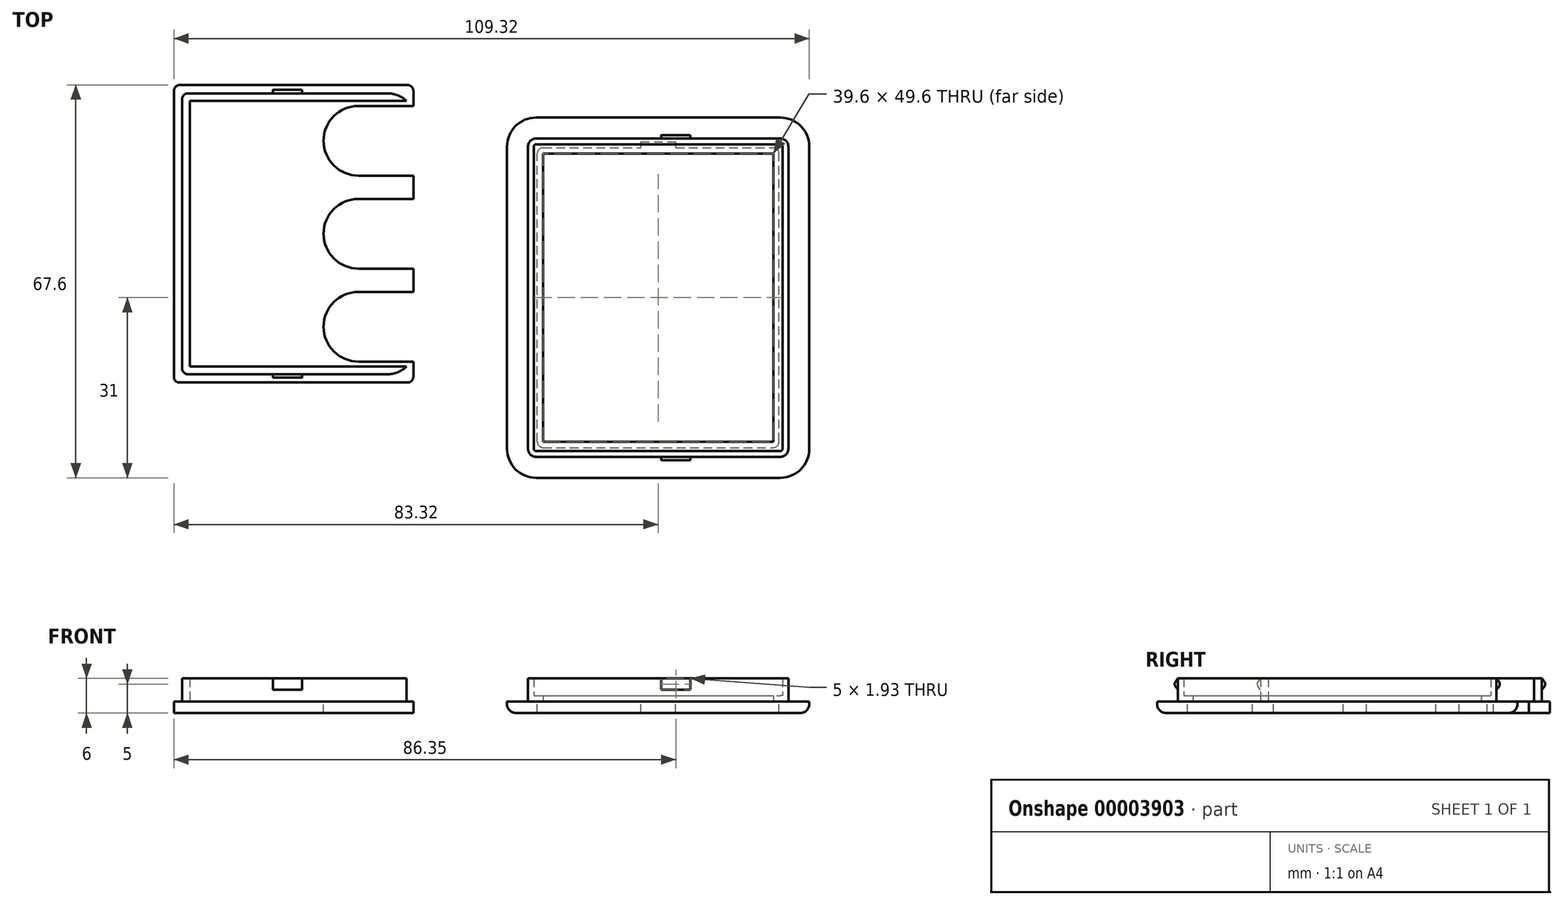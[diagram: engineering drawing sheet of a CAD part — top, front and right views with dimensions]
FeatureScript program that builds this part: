
annotation { "Feature Type Name" : "Feature", "Feature Type Description" : "" }
export const myFeature = defineFeature(function(context is Context, id is Id, definition is map)
    precondition{}
    {
        {
            var Q0;
            Q0=qCreatedBy(makeId("Top.planeOp"),FACE);
            var sketch = newSketch(context, id + "F0", { "sketchPlane" : qUnion([Q0])});
            skLineSegment(sketch, "E0.bottom", {"start": v(5, 0) * mm, "end": v(47, 0) * mm});
            skLineSegment(sketch, "E0.top", {"start": v(5, 62) * mm, "end": v(47, 62) * mm});
            skLineSegment(sketch, "E0.left", {"start": v(0, 5) * mm, "end": v(0, 57) * mm});
            skLineSegment(sketch, "E0.right", {"start": v(52, 5) * mm, "end": v(52, 57) * mm});
            skLineSegment(sketch, "E1.0", {"start": v(6.2, 56.8) * mm, "end": v(45.8, 56.8) * mm});
            skLineSegment(sketch, "E1.1", {"start": v(5.2, 6.2) * mm, "end": v(5.2, 55.8) * mm});
            skLineSegment(sketch, "E1.2", {"start": v(6.2, 5.2) * mm, "end": v(45.8, 5.2) * mm});
            skLineSegment(sketch, "E1.3", {"start": v(46.8, 6.2) * mm, "end": v(46.8, 55.8) * mm});
            skLineSegment(sketch, "E2.0", {"start": v(6.2, 55.8) * mm, "end": v(45.8, 55.8) * mm});
            skLineSegment(sketch, "E2.1", {"start": v(6.2, 6.2) * mm, "end": v(6.2, 55.8) * mm});
            skLineSegment(sketch, "E2.2", {"start": v(6.2, 6.2) * mm, "end": v(45.8, 6.2) * mm});
            skLineSegment(sketch, "E2.3", {"start": v(45.8, 6.2) * mm, "end": v(45.8, 55.8) * mm});
            skPoint(sketch, "E3.visualSharp", {"position": v(0, 62) * mm});
            skArc(sketch, "E3.filletArc", {"start": v(5, 62) * mm, "mid": v(1.46, 60.54) * mm, "end": v(0, 57) * mm});
            skPoint(sketch, "E4.visualSharp", {"position": v(52, 62) * mm});
            skArc(sketch, "E4.filletArc", {"start": v(52, 57) * mm, "mid": v(50.54, 60.54) * mm, "end": v(47, 62) * mm});
            skPoint(sketch, "E5.visualSharp", {"position": v(52, 0) * mm});
            skArc(sketch, "E5.filletArc", {"start": v(47, 0) * mm, "mid": v(50.54, 1.46) * mm, "end": v(52, 5) * mm});
            skPoint(sketch, "E6.visualSharp", {"position": v(0, 0) * mm});
            skArc(sketch, "E6.filletArc", {"start": v(0, 5) * mm, "mid": v(1.46, 1.46) * mm, "end": v(5, 0) * mm});
            skPoint(sketch, "E7.visualSharp", {"position": v(5.2, 56.8) * mm});
            skArc(sketch, "E7.filletArc", {"start": v(6.2, 56.8) * mm, "mid": v(5.5, 56.5) * mm, "end": v(5.2, 55.8) * mm});
            skPoint(sketch, "E8.visualSharp", {"position": v(46.8, 56.8) * mm});
            skArc(sketch, "E8.filletArc", {"start": v(46.8, 55.8) * mm, "mid": v(46.5, 56.5) * mm, "end": v(45.8, 56.8) * mm});
            skPoint(sketch, "E9.visualSharp", {"position": v(5.2, 5.2) * mm});
            skArc(sketch, "E9.filletArc", {"start": v(5.2, 6.2) * mm, "mid": v(5.5, 5.5) * mm, "end": v(6.2, 5.2) * mm});
            skPoint(sketch, "E10.visualSharp", {"position": v(46.8, 5.2) * mm});
            skArc(sketch, "E10.filletArc", {"start": v(45.8, 5.2) * mm, "mid": v(46.5, 5.5) * mm, "end": v(46.8, 6.2) * mm});
            skLineSegment(sketch, "E11", {"start": v(23, 56.8) * mm, "end": v(23, 57.85) * mm});
            skLineSegment(sketch, "E12", {"start": v(23, 57.85) * mm, "end": v(29, 57.85) * mm});
            skLineSegment(sketch, "E13", {"start": v(29, 57.85) * mm, "end": v(29, 56.8) * mm});
            skLineSegment(sketch, "E14", {"start": v(23, 57.85) * mm, "end": v(5.2, 57.85) * mm, "construction": true});
            skLineSegment(sketch, "E15", {"start": v(29, 57.85) * mm, "end": v(46.8, 57.85) * mm, "construction": true});
            skArc(sketch, "E16.0", {"start": v(5, 58.4) * mm, "mid": v(4.01, 57.99) * mm, "end": v(3.6, 57) * mm});
            skLineSegment(sketch, "E16.1", {"start": v(3.6, 5) * mm, "end": v(3.6, 57) * mm});
            skArc(sketch, "E16.2", {"start": v(3.6, 5) * mm, "mid": v(4.01, 4.01) * mm, "end": v(5, 3.6) * mm});
            skLineSegment(sketch, "E16.3", {"start": v(5, 3.6) * mm, "end": v(47, 3.6) * mm});
            skArc(sketch, "E16.4", {"start": v(47, 3.6) * mm, "mid": v(47.99, 4.01) * mm, "end": v(48.4, 5) * mm});
            skLineSegment(sketch, "E16.5", {"start": v(5, 58.4) * mm, "end": v(47, 58.4) * mm});
            skLineSegment(sketch, "E16.6", {"start": v(48.4, 5) * mm, "end": v(48.4, 57) * mm});
            skArc(sketch, "E16.7", {"start": v(48.4, 57) * mm, "mid": v(47.99, 57.99) * mm, "end": v(47, 58.4) * mm});
            skLineSegment(sketch, "E17.0", {"start": v(5, 57.4) * mm, "end": v(47, 57.4) * mm});
            skArc(sketch, "E17.1", {"start": v(47.4, 57) * mm, "mid": v(47.28, 57.28) * mm, "end": v(47, 57.4) * mm});
            skLineSegment(sketch, "E17.2", {"start": v(47.4, 5) * mm, "end": v(47.4, 57) * mm});
            skArc(sketch, "E17.3", {"start": v(47, 4.6) * mm, "mid": v(47.28, 4.72) * mm, "end": v(47.4, 5) * mm});
            skLineSegment(sketch, "E17.4", {"start": v(5, 4.6) * mm, "end": v(47, 4.6) * mm});
            skArc(sketch, "E17.5", {"start": v(5, 57.4) * mm, "mid": v(4.72, 57.28) * mm, "end": v(4.6, 57) * mm});
            skArc(sketch, "E17.6", {"start": v(4.6, 5) * mm, "mid": v(4.72, 4.72) * mm, "end": v(5, 4.6) * mm});
            skLineSegment(sketch, "E17.7", {"start": v(4.6, 5) * mm, "end": v(4.6, 57) * mm});
            skSolve(sketch);
        }
        {
            var Q0;
            {var subQ7=sQuery(id+"F0.wireOp",EDGE,"E12");Q0=makeQuery(id+"F0.imprint","IMPRINT",FACE,{"disambiguationData":[TD([[makeQuery(id+"F0.imprint","IMPRINT",EDGE,{"derivedFrom":subQ7}),1.0]])]});}
            var Q1;
            {var subQ5=sQuery(id+"F0.wireOp",EDGE,"E12");Q1=makeQuery(id+"F0.imprint","IMPRINT",FACE,{"disambiguationData":[TD([[makeQuery(id+"F0.imprint","IMPRINT",EDGE,{"derivedFrom":subQ5}),-1.0]])]});}
            extrude(context, id + "F1", {"entities" : qUnion([Q0, Q1]), "depth" : 4 * mm});
        }
        {
            var Q0;
            Q0=makeQuery(id+"F0.imprint","IMPRINT",FACE,{"disambiguationData":[TD([[makeQuery(id+"F0.imprint","IMPRINT",EDGE,{"derivedFrom":sQuery(id+"F0.wireOp",EDGE,"E0.bottom")}),1.0]])]});
            var Q1;
            {var subQ7=sQuery(id+"F0.wireOp",EDGE,"E12");Q1=makeQuery(id+"F0.imprint","IMPRINT",FACE,{"disambiguationData":[TD([[makeQuery(id+"F0.imprint","IMPRINT",EDGE,{"derivedFrom":subQ7}),1.0]])]});}
            var Q2;
            Q2=makeQuery(id+"F0.imprint","IMPRINT",FACE,{"disambiguationData":[TD([[makeQuery(id+"F0.imprint","IMPRINT",EDGE,{"derivedFrom":sQuery(id+"F0.wireOp",EDGE,"E1.1")}),1.0]])]});
            extrude(context, id + "F2", {"entities" : qUnion([Q0, Q1, Q2]), "operationType" : NewBodyOperationType.ADD, "oppositeDirection" : true, "depth" : 1.96 * mm});
        }
        {
            var Q0;
            Q0=makeQuery(id+"F2.opExtrude","CAP_EDGE",EDGE,{"disambiguationData":[OSD([sQuery(id+"F0.wireOp",EDGE,"E0.top")])],"isStart":false});
            var Q1;
            Q1=makeQuery(id+"F2.opExtrude","CAP_EDGE",EDGE,{"disambiguationData":[OSD([sQuery(id+"F0.wireOp",EDGE,"E4.filletArc")])],"isStart":false});
            var Q2;
            Q2=makeQuery(id+"F2.opExtrude","CAP_EDGE",EDGE,{"disambiguationData":[OSD([sQuery(id+"F0.wireOp",EDGE,"E0.right")])],"isStart":false});
            var Q3;
            Q3=makeQuery(id+"F2.opExtrude","CAP_EDGE",EDGE,{"disambiguationData":[OSD([sQuery(id+"F0.wireOp",EDGE,"E5.filletArc")])],"isStart":false});
            var Q4;
            Q4=makeQuery(id+"F2.opExtrude","CAP_EDGE",EDGE,{"disambiguationData":[OSD([sQuery(id+"F0.wireOp",EDGE,"E0.bottom")])],"isStart":false});
            var Q5;
            Q5=makeQuery(id+"F2.opExtrude","CAP_EDGE",EDGE,{"disambiguationData":[OSD([sQuery(id+"F0.wireOp",EDGE,"E3.filletArc")])],"isStart":false});
            var Q6;
            Q6=makeQuery(id+"F2.opExtrude","CAP_EDGE",EDGE,{"disambiguationData":[OSD([sQuery(id+"F0.wireOp",EDGE,"E0.left")])],"isStart":false});
            var Q7;
            Q7=makeQuery(id+"F2.opExtrude","CAP_EDGE",EDGE,{"disambiguationData":[OSD([sQuery(id+"F0.wireOp",EDGE,"E6.filletArc")])],"isStart":false});
            fillet(context, id + "F3", {"entities" : qUnion([Q0, Q1, Q2, Q3, Q4, Q5, Q6, Q7]), "radius" : 1.5 * mm, "tangentPropagation" : true, "allowEdgeOverflow" : false});
        }
        {
            var Q0;
            Q0=makeQuery(id+"F0.imprint","IMPRINT",FACE,{"disambiguationData":[TD([[makeQuery(id+"F0.imprint","IMPRINT",EDGE,{"derivedFrom":sQuery(id+"F0.wireOp",EDGE,"E1.1")}),-1.0]])]});
            var Q1;
            Q1=makeQuery(id+"F0.imprint","IMPRINT",FACE,{"disambiguationData":[TD([[makeQuery(id+"F0.imprint","IMPRINT",EDGE,{"derivedFrom":sQuery(id+"F0.wireOp",EDGE,"E1.1")}),1.0]])]});
            var Q2;
            {var subQ3=sQuery(id+"F0.wireOp",EDGE,"E11");var subQ5=sQuery(id+"F0.wireOp",EDGE,"E1.0");var subQ7=makeQuery(id+"F0.imprint","INTERSECT",VERTEX,{"derivedFrom":[subQ5,subQ3]});Q2=makeQuery(id+"F0.imprint","IMPRINT",FACE,{"disambiguationData":[TD([[makeQuery(id+"F0.imprint","IMPRINT",EDGE,{"disambiguationData":[TD([[subQ7,-1.0]])],"derivedFrom":subQ5}),1.0]])]});}
            extrude(context, id + "F4", {"entities" : qUnion([Q0, Q1, Q2]), "operationType" : NewBodyOperationType.ADD, "depth" : 1 * mm});
        }
        {
            var Q0;
            Q0=qCreatedBy(makeId("Top.planeOp"),FACE);
            var sketch = newSketch(context, id + "F5", { "sketchPlane" : qUnion([Q0])});
            skLineSegment(sketch, "E18.bottom", {"start": v(-56.32, 16.4) * mm, "end": v(-17.12, 16.4) * mm});
            skLineSegment(sketch, "E18.top", {"start": v(-56.32, 67.6) * mm, "end": v(-17.12, 67.6) * mm});
            skLineSegment(sketch, "E18.left", {"start": v(-57.32, 17.4) * mm, "end": v(-57.32, 66.6) * mm});
            skLineSegment(sketch, "E18.right", {"start": v(-16.12, 17.4) * mm, "end": v(-16.12, 66.6) * mm});
            skLineSegment(sketch, "E19.0", {"start": v(-55.24, 18.47) * mm, "end": v(-55.24, 65.52) * mm, "construction": true});
            skLineSegment(sketch, "E19.1", {"start": v(-55.24, 18.47) * mm, "end": v(-17.29, 18.47) * mm, "construction": true});
            skLineSegment(sketch, "E19.3", {"start": v(-55.24, 65.52) * mm, "end": v(-17.29, 65.52) * mm, "construction": true});
            skLineSegment(sketch, "E20.0", {"start": v(-54.6, 64.87) * mm, "end": v(-17.29, 64.87) * mm});
            skLineSegment(sketch, "E20.1", {"start": v(-54.6, 19.12) * mm, "end": v(-54.6, 64.87) * mm});
            skLineSegment(sketch, "E20.2", {"start": v(-54.6, 19.12) * mm, "end": v(-17.29, 19.12) * mm});
            skLineSegment(sketch, "E21.0", {"start": v(-54.9, 66.17) * mm, "end": v(-17.29, 66.17) * mm});
            skLineSegment(sketch, "E21.1", {"start": v(-55.9, 18.82) * mm, "end": v(-55.9, 65.17) * mm});
            skLineSegment(sketch, "E21.2", {"start": v(-54.9, 17.82) * mm, "end": v(-17.29, 17.82) * mm});
            skLineSegment(sketch, "E22", {"start": v(-17.29, 17.82) * mm, "end": v(-17.29, 19.12) * mm});
            skLineSegment(sketch, "E23", {"start": v(-17.29, 64.87) * mm, "end": v(-17.29, 66.17) * mm});
            skLineSegment(sketch, "E24", {"start": v(-57.32, 42) * mm, "end": v(-31.57, 42) * mm, "construction": true});
            skLineSegment(sketch, "E25.bottom", {"start": v(-25.57, 36) * mm, "end": v(-16.12, 36) * mm});
            skLineSegment(sketch, "E25.top", {"start": v(-25.57, 48) * mm, "end": v(-16.12, 48) * mm});
            skLineSegment(sketch, "E25.left", {"start": v(-31.57, 42) * mm, "end": v(-31.57, 42) * mm});
            skLineSegment(sketch, "E25.right", {"start": v(-16.12, 36) * mm, "end": v(-16.12, 48) * mm});
            skLineSegment(sketch, "E26.1.0.0", {"start": v(-31.57, 26) * mm, "end": v(-31.57, 26) * mm});
            skLineSegment(sketch, "E26.1.0.1", {"start": v(-25.57, 20) * mm, "end": v(-16.12, 20) * mm});
            skLineSegment(sketch, "E26.1.0.2", {"start": v(-25.57, 32) * mm, "end": v(-16.12, 32) * mm});
            skLineSegment(sketch, "E26.direction1", {"start": v(-31.57, 36) * mm, "end": v(-31.57, 20) * mm, "construction": true});
            skLineSegment(sketch, "E27.1.0.0", {"start": v(-31.57, 58) * mm, "end": v(-31.57, 58) * mm});
            skLineSegment(sketch, "E27.1.0.1", {"start": v(-25.57, 52) * mm, "end": v(-16.12, 52) * mm});
            skLineSegment(sketch, "E27.1.0.2", {"start": v(-25.57, 64) * mm, "end": v(-16.12, 64) * mm});
            skLineSegment(sketch, "E27.direction1", {"start": v(-31.57, 36) * mm, "end": v(-31.57, 52) * mm, "construction": true});
            skPoint(sketch, "E28.visualSharp", {"position": v(-31.57, 20) * mm});
            skArc(sketch, "E28.filletArc", {"start": v(-31.57, 26) * mm, "mid": v(-29.8, 21.75) * mm, "end": v(-25.57, 20) * mm});
            skPoint(sketch, "E29.visualSharp", {"position": v(-31.57, 32) * mm});
            skArc(sketch, "E29.filletArc", {"start": v(-25.57, 32) * mm, "mid": v(-29.8, 30.24) * mm, "end": v(-31.57, 26) * mm});
            skPoint(sketch, "E30.visualSharp", {"position": v(-31.57, 36) * mm});
            skArc(sketch, "E30.filletArc", {"start": v(-31.57, 42) * mm, "mid": v(-29.8, 37.75) * mm, "end": v(-25.57, 36) * mm});
            skPoint(sketch, "E31.visualSharp", {"position": v(-31.57, 48) * mm});
            skArc(sketch, "E31.filletArc", {"start": v(-25.57, 48) * mm, "mid": v(-29.8, 46.24) * mm, "end": v(-31.57, 42) * mm});
            skPoint(sketch, "E32.visualSharp", {"position": v(-31.57, 52) * mm});
            skArc(sketch, "E32.filletArc", {"start": v(-31.57, 58) * mm, "mid": v(-29.8, 53.75) * mm, "end": v(-25.57, 52) * mm});
            skPoint(sketch, "E33.visualSharp", {"position": v(-31.57, 64) * mm});
            skArc(sketch, "E33.filletArc", {"start": v(-25.57, 64) * mm, "mid": v(-29.8, 62.24) * mm, "end": v(-31.57, 58) * mm});
            skPoint(sketch, "E34.visualSharp", {"position": v(-57.32, 16.4) * mm});
            skArc(sketch, "E34.filletArc", {"start": v(-57.32, 17.4) * mm, "mid": v(-57.02, 16.7) * mm, "end": v(-56.32, 16.4) * mm});
            skPoint(sketch, "E35.visualSharp", {"position": v(-16.12, 16.4) * mm});
            skArc(sketch, "E35.filletArc", {"start": v(-17.12, 16.4) * mm, "mid": v(-16.4, 16.7) * mm, "end": v(-16.12, 17.4) * mm});
            skPoint(sketch, "E36.visualSharp", {"position": v(-57.32, 67.6) * mm});
            skArc(sketch, "E36.filletArc", {"start": v(-56.32, 67.6) * mm, "mid": v(-57.02, 67.3) * mm, "end": v(-57.32, 66.6) * mm});
            skPoint(sketch, "E37.visualSharp", {"position": v(-16.12, 67.6) * mm});
            skArc(sketch, "E37.filletArc", {"start": v(-16.12, 66.6) * mm, "mid": v(-16.4, 67.3) * mm, "end": v(-17.12, 67.6) * mm});
            skPoint(sketch, "E38.visualSharp", {"position": v(-55.9, 66.17) * mm});
            skArc(sketch, "E38.filletArc", {"start": v(-54.9, 66.17) * mm, "mid": v(-55.6, 65.88) * mm, "end": v(-55.9, 65.17) * mm});
            skPoint(sketch, "E39.visualSharp", {"position": v(-55.9, 17.82) * mm});
            skArc(sketch, "E39.filletArc", {"start": v(-55.9, 18.82) * mm, "mid": v(-55.6, 18.12) * mm, "end": v(-54.9, 17.82) * mm});
            skSolve(sketch);
        }
        {
            var Q0;
            Q0=makeQuery(id+"F5.imprint","IMPRINT",FACE,{"disambiguationData":[TD([[makeQuery(id+"F5.imprint","IMPRINT",EDGE,{"derivedFrom":sQuery(id+"F5.wireOp",EDGE,"E20.0")}),1.0]])]});
            extrude(context, id + "F6", {"entities" : qUnion([Q0]), "depth" : 4 * mm});
        }
        {
            var Q0;
            Q0=makeQuery(id+"F5.imprint","IMPRINT",FACE,{"disambiguationData":[TD([[makeQuery(id+"F5.imprint","IMPRINT",EDGE,{"derivedFrom":sQuery(id+"F5.wireOp",EDGE,"E18.bottom")}),1.0]])]});
            var Q1;
            Q1=makeQuery(id+"F5.imprint","IMPRINT",FACE,{"disambiguationData":[TD([[makeQuery(id+"F5.imprint","IMPRINT",EDGE,{"derivedFrom":sQuery(id+"F5.wireOp",EDGE,"E20.0")}),1.0]])]});
            extrude(context, id + "F7", {"entities" : qUnion([Q0, Q1]), "operationType" : NewBodyOperationType.ADD, "oppositeDirection" : true, "depth" : 2 * mm});
        }
        {
            var Q0;
            Q0=makeQuery(id+"F6.opExtrude","SWEPT_EDGE",EDGE,{"disambiguationData":[OSD([sQuery(id+"F5.wireOp",EDGE,"E21.0"),sQuery(id+"F5.wireOp",EDGE,"E23")])]});
            var Q1;
            Q1=makeQuery(id+"F6.opExtrude","SWEPT_EDGE",EDGE,{"disambiguationData":[OSD([sQuery(id+"F5.wireOp",EDGE,"E21.2"),sQuery(id+"F5.wireOp",EDGE,"E22")])]});
            fillet(context, id + "F8", {"entities" : qUnion([Q0, Q1]), "radius" : 5 * mm, "tangentPropagation" : true, "allowEdgeOverflow" : false});
        }
        {
            var Q0;
            Q0=makeQuery(id+"F6.opExtrude","SWEPT_FACE",FACE,{"disambiguationData":[OSD([sQuery(id+"F5.wireOp",EDGE,"E21.2")])]});
            var sketch = newSketch(context, id + "F9", { "sketchPlane" : qUnion([Q0])});
            skLineSegment(sketch, "E40", {"start": v(-37.77, 4) * mm, "end": v(-37.77, 0) * mm, "construction": true});
            skLineSegment(sketch, "E41.bottom", {"start": v(-40.27, 2) * mm, "end": v(-35.27, 2) * mm});
            skLineSegment(sketch, "E41.left", {"start": v(-40.27, 2) * mm, "end": v(-40.27, 4) * mm});
            skLineSegment(sketch, "E41.right", {"start": v(-35.27, 2) * mm, "end": v(-35.27, 4) * mm});
            skPoint(sketch, "E41.middle", {"position": v(-37.77, 4) * mm});
            skLineSegment(sketch, "E42.0", {"start": v(-54.9, 4) * mm, "end": v(-20.65, 4) * mm, "construction": true});
            skSolve(sketch);
        }
        {
            var Q0;
            Q0=makeQuery(id+"F6.opExtrude","SWEPT_FACE",FACE,{"disambiguationData":[OSD([sQuery(id+"F5.wireOp",EDGE,"E21.1")])]});
            var Q1;
            Q1=sQuery(id+"F9.wireOp",VERTEX,"E41.bottom.start");
            cPlane(context, id + "F10", {"entities" : qUnion([Q0, Q1]), "cplaneType" : CPlaneType.PLANE_POINT, "offset" : 25 * mm, "width" : 150 * mm, "height" : 150 * mm});
        }
        {
            var Q0;
            Q0=qCreatedBy(id+"F10.planeOp",FACE);
            var sketch = newSketch(context, id + "F11", { "sketchPlane" : qUnion([Q0])});
            skPoint(sketch, "E43.0", {"position": v(-17.82, 2) * mm});
            skPoint(sketch, "E43.1", {"position": v(-17.82, 4) * mm});
            skLineSegment(sketch, "E44", {"start": v(-17.82, 4) * mm, "end": v(-17.82, 2) * mm});
            skLineSegment(sketch, "E45", {"start": v(-17.82, 3) * mm, "end": v(-17.02, 3) * mm, "construction": true});
            skLineSegment(sketch, "E46", {"start": v(-17.82, 2) * mm, "end": v(-17.02, 3) * mm});
            skLineSegment(sketch, "E47", {"start": v(-17.82, 4) * mm, "end": v(-17.02, 3) * mm});
            skSolve(sketch);
        }
        {
            var Q0;
            Q0 = qSketchRegion(id + "F11", true);
            var Q1;
            Q1=sQuery(id+"F9.wireOp",VERTEX,"E41.right.start");
            extrude(context, id + "F12", {"entities" : qUnion([Q0]), "endBound" : BoundingType.UP_TO_VERTEX, "oppositeDirection" : true, "endBoundEntityVertex" : qUnion([Q1]), "depth" : 25 * mm});
        }
        {
            var Q0;
            Q0=makeQuery(id+"F12.opExtrude","SWEPT_EDGE",EDGE,{"disambiguationData":[OSD([sQuery(id+"F11.wireOp",EDGE,"sKzuGCaV-Tl3E-rwEO-ntCV-wSZY4JM2qxc9"),sQuery(id+"F11.wireOp",EDGE,"4RffTHSf-Eqzv-J231-T1bQ-UyBnTeHLe6Go")])]});
            var Q1;
            Q1=makeQuery(id+"F12.opExtrude","SWEPT_EDGE",EDGE,{"disambiguationData":[OSD([sQuery(id+"F11.wireOp",EDGE,"2TYR6BhU-d14F-oxGB-XzqQ-LSk6sUKBAC2f"),sQuery(id+"F11.wireOp",EDGE,"3Tv0drpj-AehL-vRw2-5iAH-hhYOkTaRpjAx")])]});
            var Q2;
            Q2=makeQuery(id+"F12.opExtrude","SWEPT_EDGE",EDGE,{"disambiguationData":[OSD([sQuery(id+"F11.wireOp",EDGE,"E46"),sQuery(id+"F11.wireOp",EDGE,"E47")])]});
            fillet(context, id + "F13", {"entities" : qUnion([Q0, Q1, Q2]), "radius" : 0.7 * mm, "tangentPropagation" : true, "allowEdgeOverflow" : false});
        }
        {
            var Q0;
            Q0=sQuery(id+"F5.wireOp",VERTEX,"E30.filletArc.center");
            var Q1;
            Q1=qCreatedBy(makeId("Front.planeOp"),FACE);
            cPlane(context, id + "F14", {"entities" : qUnion([Q0, Q1]), "cplaneType" : CPlaneType.PLANE_POINT, "offset" : 25 * mm, "width" : 150 * mm, "height" : 150 * mm});
        }
        {
            var Q0;
            Q0=makeQuery(id+"F12.opExtrude","SWEPT_BODY",BODY,{"disambiguationData":[OSD([sQuery(id+"F11.wireOp",EDGE,"E44"),sQuery(id+"F11.wireOp",EDGE,"E46"),sQuery(id+"F11.wireOp",EDGE,"E47")])]});
            var Q1;
            Q1=qCreatedBy(id+"F14.planeOp",FACE);
            mirror(context, id + "F15", {"entities" : qUnion([Q0]), "mirrorPlane" : qUnion([Q1])});
        }
        {
            var Q0;
            Q0=makeQuery(id+"F15.opPattern","COPY",BODY,{"derivedFrom":makeQuery(id+"F12.opExtrude","SWEPT_BODY",BODY,{"disambiguationData":[OSD([sQuery(id+"F11.wireOp",EDGE,"E44"),sQuery(id+"F11.wireOp",EDGE,"E46"),sQuery(id+"F11.wireOp",EDGE,"E47")])]}),"instanceName":"1"});
            transform(context, id + "F16", {"entities" : qUnion([Q0]), "transformType" : TransformType.TRANSLATION_3D, "dx" : 66.8 * mm, "dy" : -7.8 * mm, "dz" : 0 * mm, "makeCopy" : true});
        }
        {
            var Q0;
            Q0=sQuery(id+"F0.wireOp",EDGE,"E0.right");
            cPoint(context, id + "F17", {"entities" : qUnion([Q0]), "parameter" : 0.5});
        }
        {
            var Q0;
            Q0=qCreatedBy(id+"F14.planeOp",FACE);
            var Q1;
            Q1 = qCreatedBy(id + "F17" ,VERTEX);
            cPlane(context, id + "F18", {"entities" : qUnion([Q0, Q1]), "cplaneType" : CPlaneType.PLANE_POINT, "offset" : 25 * mm, "width" : 150 * mm, "height" : 150 * mm});
        }
        {
            var Q0;
            Q0=makeQuery(id+"F16.opPattern","COPY",BODY,{"derivedFrom":makeQuery(id+"F15.opPattern","COPY",BODY,{"derivedFrom":makeQuery(id+"F12.opExtrude","SWEPT_BODY",BODY,{"disambiguationData":[OSD([sQuery(id+"F11.wireOp",EDGE,"E44"),sQuery(id+"F11.wireOp",EDGE,"E46"),sQuery(id+"F11.wireOp",EDGE,"E47")])]}),"instanceName":"1"}),"instanceName":"1"});
            var Q1;
            Q1=qCreatedBy(id+"F18.planeOp",FACE);
            mirror(context, id + "F19", {"operationType" : NewBodyOperationType.ADD, "entities" : qUnion([Q0]), "mirrorPlane" : qUnion([Q1])});
        }
    });
